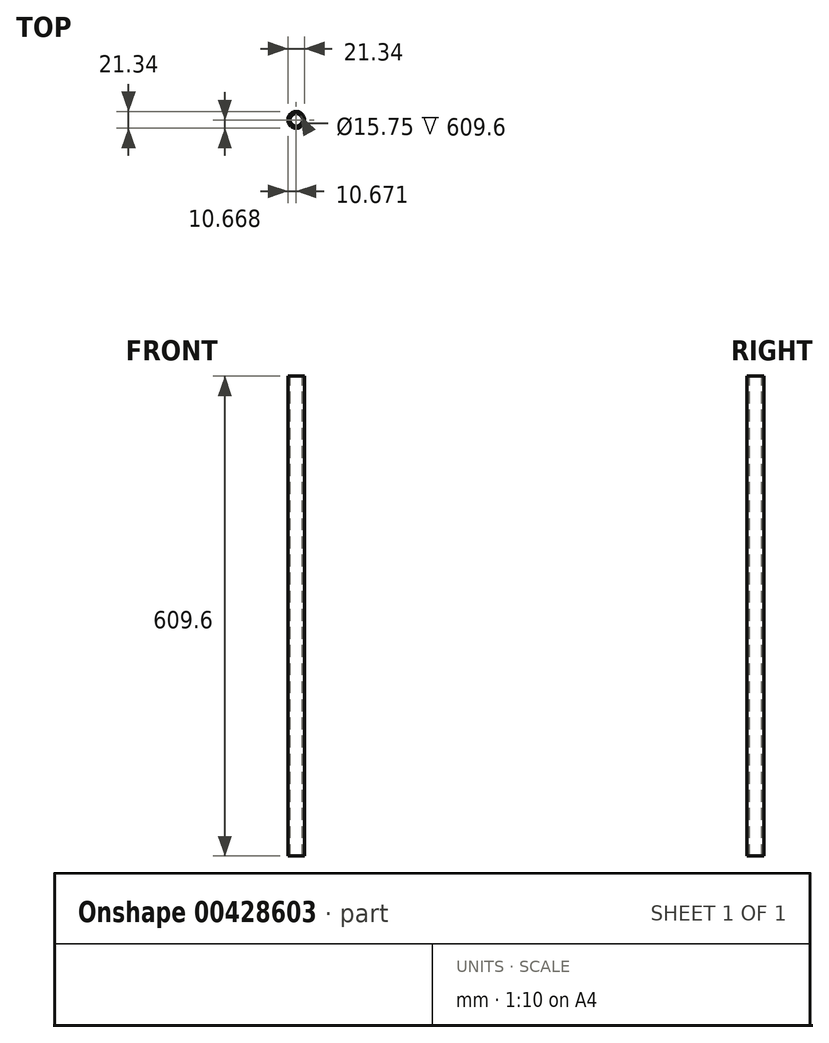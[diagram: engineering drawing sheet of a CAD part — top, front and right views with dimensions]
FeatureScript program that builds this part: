
annotation { "Feature Type Name" : "Feature", "Feature Type Description" : "" }
export const myFeature = defineFeature(function(context is Context, id is Id, definition is map)
    precondition{}
    {
        {
            var Q0;
            Q0=qCreatedBy(makeId("Top.planeOp"),FACE);
            var sketch = newSketch(context, id + "F0", { "sketchPlane" : qUnion([Q0])});
            skCircle(sketch, "E0", {"center": v(72.06, 47.03) * mm, "radius": 10.67 * mm});
            skSolve(sketch);
        }
        {
            var Q0;
            Q0=makeQuery(id+"F0.imprint","IMPRINT",FACE,{"disambiguationData":[TD([[makeQuery(id+"F0.imprint","IMPRINT",EDGE,{"derivedFrom":sQuery(id+"F0.wireOp",EDGE,"E0")}),1.0]])]});
            var sketch = newSketch(context, id + "F1", { "sketchPlane" : qUnion([Q0])});
            skCircle(sketch, "E1", {"center": v(72.06, 47.03) * mm, "radius": 7.87 * mm});
            skSolve(sketch);
        }
        {
            var Q0;
            Q0=makeQuery(id+"F1.imprint","IMPRINT",FACE,{"disambiguationData":[TD([[makeQuery(id+"F1.imprint","IMPRINT",EDGE,{"derivedFrom":sQuery(id+"F1.wireOp",EDGE,"E1")}),-1.0]])]});
            extrude(context, id + "F2", {"entities" : qUnion([Q0]), "oppositeDirection" : true, "depth" : 609.6 * mm});
        }
    });
